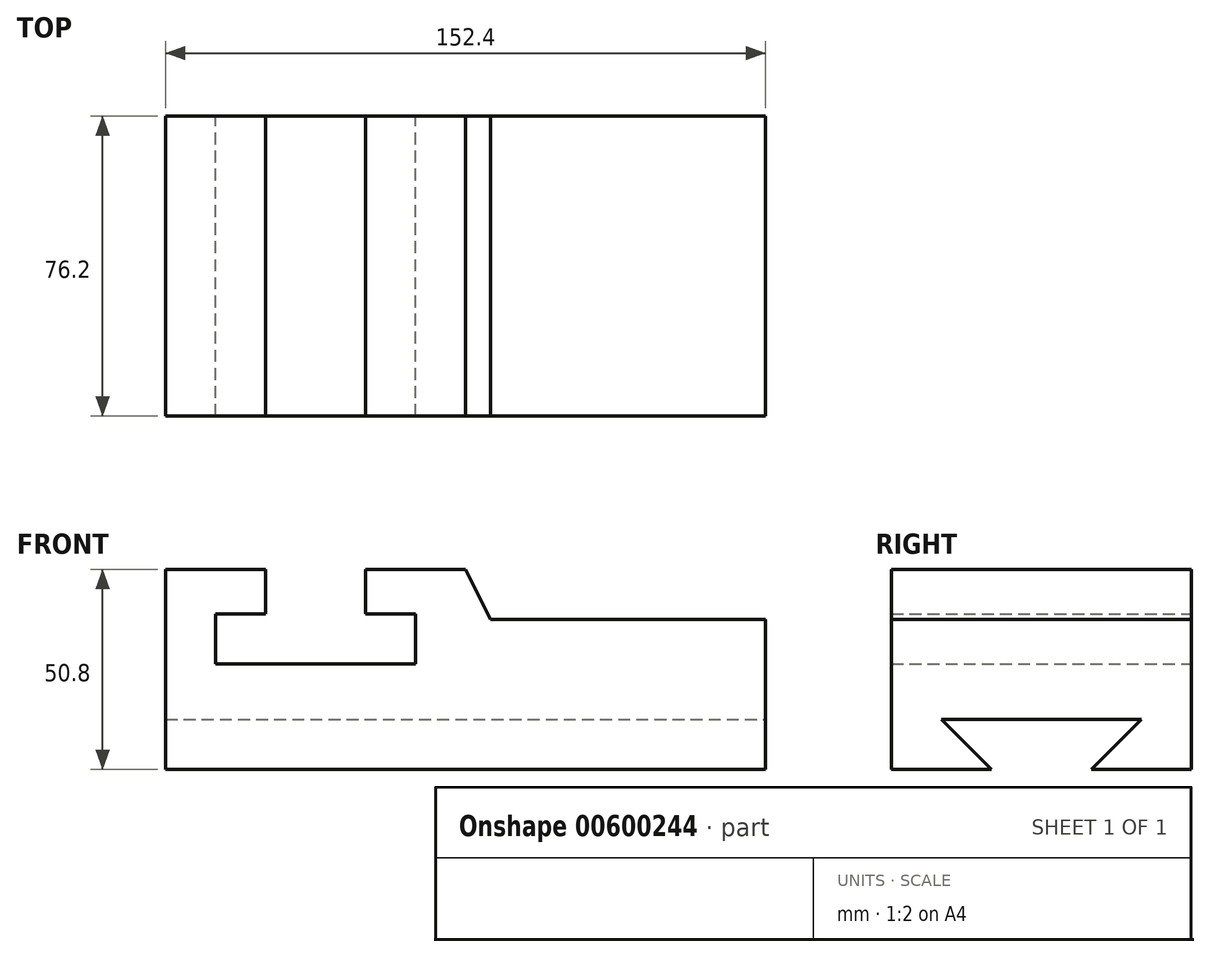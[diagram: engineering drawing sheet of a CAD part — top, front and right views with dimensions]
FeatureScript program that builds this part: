
annotation { "Feature Type Name" : "Feature", "Feature Type Description" : "" }
export const myFeature = defineFeature(function(context is Context, id is Id, definition is map)
    precondition{}
    {
        {
            var Q0;
            Q0=qCreatedBy(makeId("Front.planeOp"),FACE);
            var sketch = newSketch(context, id + "F0", { "sketchPlane" : qUnion([Q0])});
            skLineSegment(sketch, "E0", {"start": v(0, 63.16) * mm, "end": v(25.4, 63.16) * mm});
            skLineSegment(sketch, "E1", {"start": v(25.4, 63.16) * mm, "end": v(25.4, 51.84) * mm});
            skLineSegment(sketch, "E2", {"start": v(25.4, 51.84) * mm, "end": v(12.7, 51.84) * mm});
            skLineSegment(sketch, "E3", {"start": v(12.7, 51.84) * mm, "end": v(12.7, 39.14) * mm});
            skLineSegment(sketch, "E4", {"start": v(12.7, 39.14) * mm, "end": v(63.5, 39.14) * mm});
            skLineSegment(sketch, "E5", {"start": v(63.5, 39.14) * mm, "end": v(63.5, 51.84) * mm});
            skLineSegment(sketch, "E6", {"start": v(63.5, 51.84) * mm, "end": v(50.8, 51.84) * mm});
            skLineSegment(sketch, "E7", {"start": v(50.8, 51.84) * mm, "end": v(50.8, 63.16) * mm});
            skLineSegment(sketch, "E8", {"start": v(50.8, 63.16) * mm, "end": v(76.2, 63.16) * mm});
            skLineSegment(sketch, "E9", {"start": v(76.2, 63.16) * mm, "end": v(82.55, 50.46) * mm});
            skLineSegment(sketch, "E10", {"start": v(82.55, 50.46) * mm, "end": v(152.4, 50.46) * mm});
            skLineSegment(sketch, "E11", {"start": v(152.4, 50.46) * mm, "end": v(152.4, 12.36) * mm});
            skLineSegment(sketch, "E12", {"start": v(152.4, 12.36) * mm, "end": v(0, 12.36) * mm});
            skLineSegment(sketch, "E13", {"start": v(0, 12.36) * mm, "end": v(0, 63.16) * mm});
            skSolve(sketch);
        }
        {
            var Q0;
            Q0=makeQuery(id+"F0.imprint","IMPRINT",FACE,{"disambiguationData":[TD([[makeQuery(id+"F0.imprint","IMPRINT",EDGE,{"derivedFrom":sQuery(id+"F0.wireOp",EDGE,"E0")}),-1.0]])]});
            extrude(context, id + "F1", {"entities" : qUnion([Q0]), "depth" : 76.2 * mm, "offsetDistance" : 25.4 * mm});
        }
        {
            var Q0;
            Q0=makeQuery(id+"F1.opExtrude","SWEPT_FACE",FACE,{"disambiguationData":[OSD([sQuery(id+"F0.wireOp",EDGE,"E11")])]});
            var sketch = newSketch(context, id + "F2", { "sketchPlane" : qUnion([Q0])});
            skLineSegment(sketch, "E14", {"start": v(-50.8, 12.36) * mm, "end": v(-63.5, 25.06) * mm});
            skLineSegment(sketch, "E15", {"start": v(-63.5, 25.06) * mm, "end": v(-12.7, 25.06) * mm});
            skLineSegment(sketch, "E16", {"start": v(-12.7, 25.06) * mm, "end": v(-25.4, 12.36) * mm});
            skSolve(sketch);
        }
        {
            var Q0;
            Q0 = qSketchRegion(id + "F2", true);
            var Q1;
            {var subQ0=sQuery(id+"F2.wireOp",EDGE,"E14");Q1=makeQuery(id+"F2.imprint","IMPRINT",FACE,{"disambiguationData":[TD([[makeQuery(id+"F2.imprint","IMPRINT",EDGE,{"derivedFrom":subQ0}),-1.0]])]});}
            extrude(context, id + "F3", {"entities" : qUnion([Q0, Q1]), "operationType" : NewBodyOperationType.REMOVE, "oppositeDirection" : true, "depth" : 152.4 * mm, "offsetDistance" : 25.4 * mm});
        }
    });
